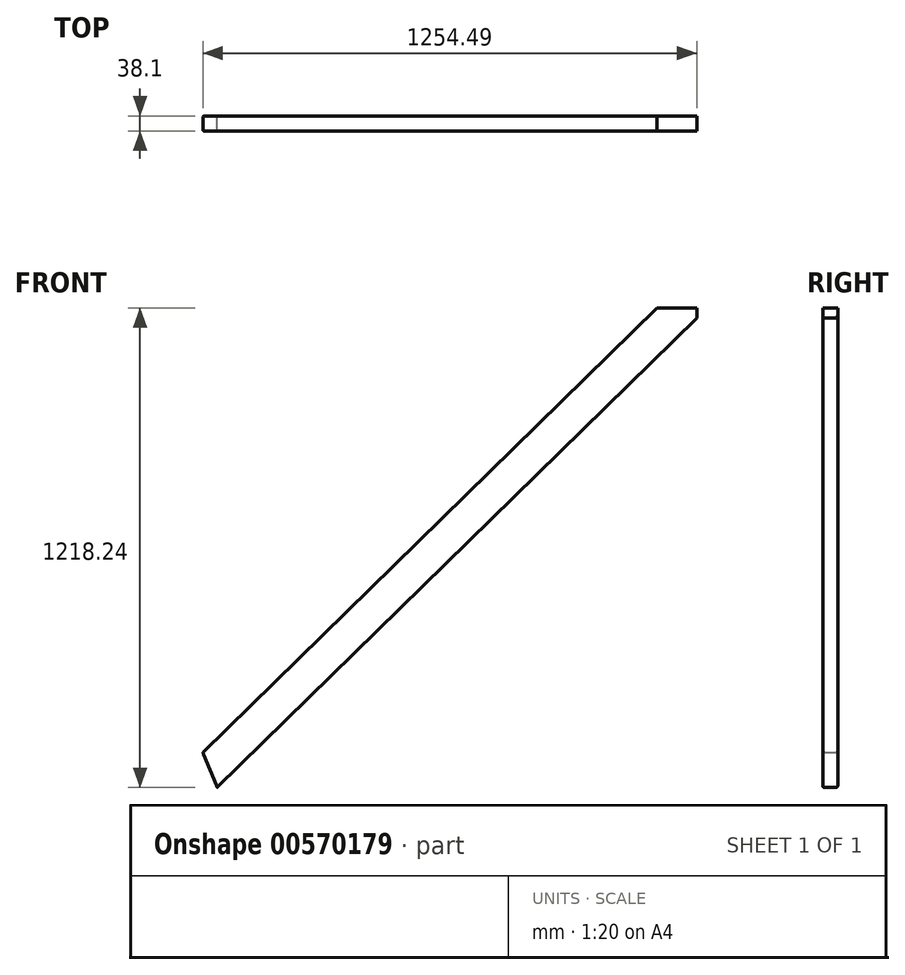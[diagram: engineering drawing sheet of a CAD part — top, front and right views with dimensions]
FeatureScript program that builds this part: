
annotation { "Feature Type Name" : "Feature", "Feature Type Description" : "" }
export const myFeature = defineFeature(function(context is Context, id is Id, definition is map)
    precondition{}
    {
        {
            var Q0;
            Q0=qCreatedBy(makeId("Front.planeOp"),FACE);
            var sketch = newSketch(context, id + "F0", { "sketchPlane" : qUnion([Q0])});
            skLineSegment(sketch, "E0", {"start": v(135.56, -189.86) * mm, "end": v(1288.92, 939.48) * mm});
            skLineSegment(sketch, "E1", {"start": v(171.83, -278.76) * mm, "end": v(1390.05, 914.08) * mm});
            skLineSegment(sketch, "E2", {"start": v(1390.05, 914.08) * mm, "end": v(1390.05, 939.48) * mm});
            skLineSegment(sketch, "E3", {"start": v(1288.92, 939.48) * mm, "end": v(1390.05, 939.48) * mm});
            skLineSegment(sketch, "E4", {"start": v(135.56, -189.86) * mm, "end": v(171.83, -278.76) * mm});
            skSolve(sketch);
        }
        {
            var Q0;
            Q0 = qSketchRegion(id + "F0", true);
            extrude(context, id + "F1", {"entities" : qUnion([Q0]), "depth" : 38.1 * mm, "offsetDistance" : 25.4 * mm});
        }
        {
            var Q0;
            Q0=makeQuery(id+"F1.opExtrude","CAP_EDGE",EDGE,{"disambiguationData":[OSD([sQuery(id+"F0.wireOp",EDGE,"E0")])],"isStart":false});
            var Q1;
            Q1=makeQuery(id+"F1.opExtrude","CAP_EDGE",EDGE,{"disambiguationData":[OSD([sQuery(id+"F0.wireOp",EDGE,"E0")])],"isStart":true});
            var Q2;
            Q2=makeQuery(id+"F1.opExtrude","CAP_EDGE",EDGE,{"disambiguationData":[OSD([sQuery(id+"F0.wireOp",EDGE,"E1")])],"isStart":false});
            fillet(context, id + "F2", {"entities" : qUnion([Q0, Q1, Q2]), "radius" : 5.08 * mm, "tangentPropagation" : true, "allowEdgeOverflow" : false});
        }
        {
            var Q0;
            Q0=makeQuery(id+"F1.opExtrude","CAP_EDGE",EDGE,{"disambiguationData":[OSD([sQuery(id+"F0.wireOp",EDGE,"E1")])],"isStart":true});
            fillet(context, id + "F3", {"entities" : qUnion([Q0]), "radius" : 5.08 * mm, "tangentPropagation" : true, "allowEdgeOverflow" : false});
        }
    });
